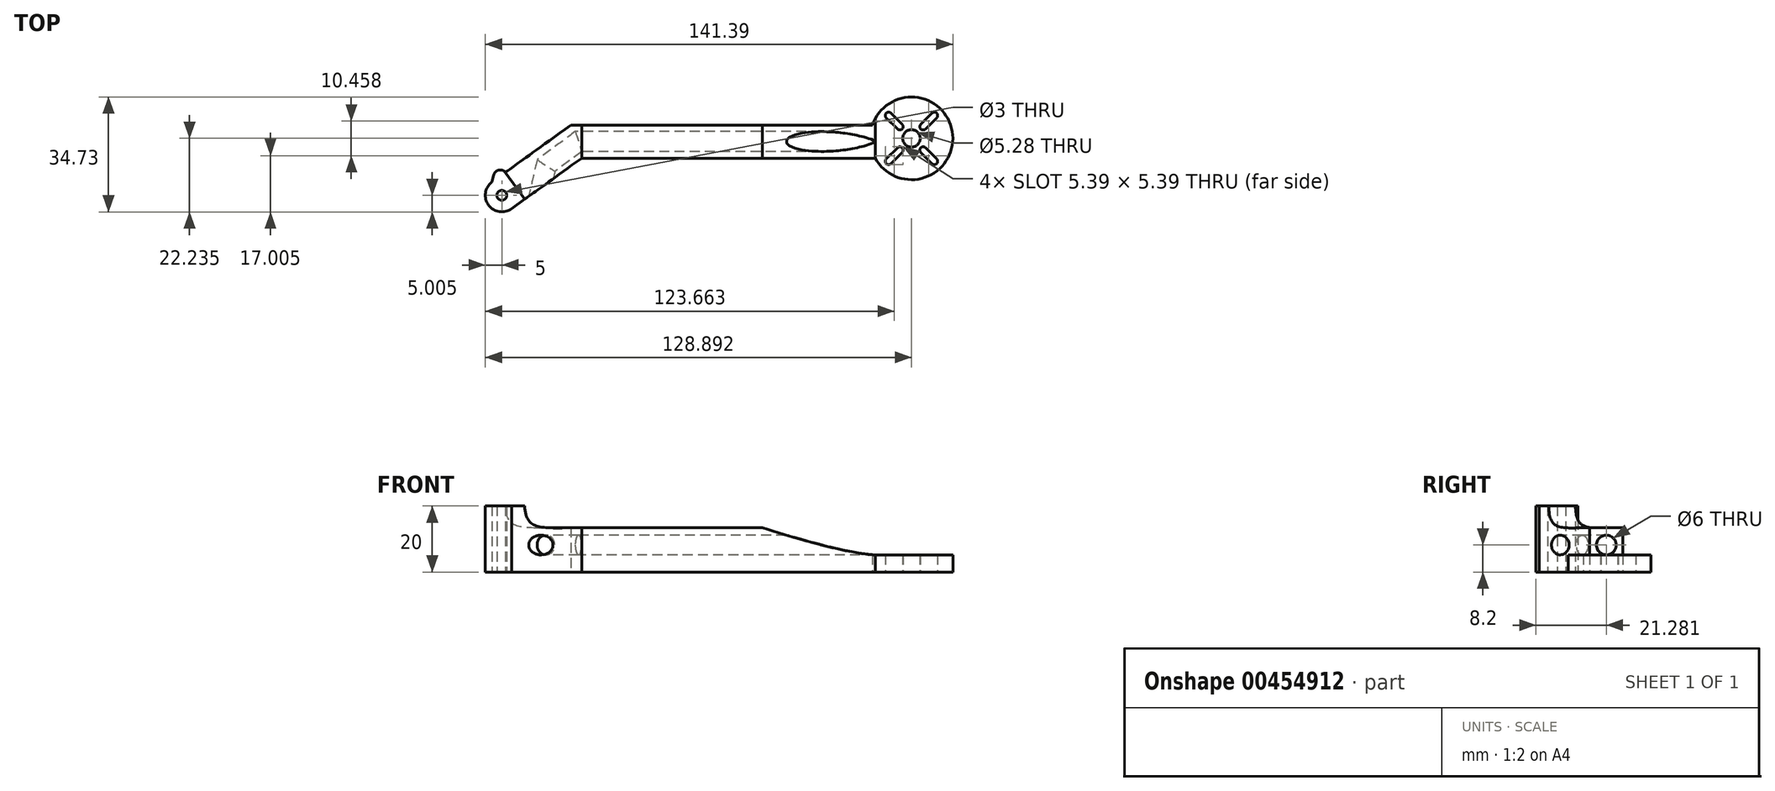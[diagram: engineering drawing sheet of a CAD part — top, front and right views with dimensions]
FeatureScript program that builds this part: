
annotation { "Feature Type Name" : "Feature", "Feature Type Description" : "" }
export const myFeature = defineFeature(function(context is Context, id is Id, definition is map)
    precondition{}
    {
        {
            var Q0;
            Q0=qCreatedBy(makeId("Top.planeOp"),FACE);
            var sketch = newSketch(context, id + "F0", { "sketchPlane" : qUnion([Q0])});
            skLineSegment(sketch, "E0", {"start": v(-161.05, 41.93) * mm, "end": v(-137.16, 59.15) * mm, "construction": true});
            skLineSegment(sketch, "E1", {"start": v(-137.16, 59.15) * mm, "end": v(-37.16, 59.15) * mm, "construction": true});
            skArc(sketch, "E2", {"start": v(-48.13, 53.17) * mm, "mid": v(-24.7, 60.23) * mm, "end": v(-49, 63.17) * mm});
            skLineSegment(sketch, "E3.0", {"start": v(-158.07, 37.9) * mm, "end": v(-136.9, 53.17) * mm});
            skLineSegment(sketch, "E4.0", {"start": v(-164.03, 45.94) * mm, "end": v(-140.14, 63.17) * mm});
            skArc(sketch, "E5", {"start": v(-164.03, 45.94) * mm, "mid": v(-165.07, 38.95) * mm, "end": v(-158.07, 37.9) * mm});
            skLineSegment(sketch, "E6", {"start": v(-140.14, 63.17) * mm, "end": v(-49, 63.17) * mm});
            skLineSegment(sketch, "E7", {"start": v(-136.9, 53.17) * mm, "end": v(-48.13, 53.17) * mm});
            skCircle(sketch, "E8", {"center": v(-37.16, 59.15) * mm, "radius": 2.64 * mm});
            skArc(sketch, "E9.0.startCap", {"start": v(-44.79, 65.37) * mm, "mid": v(-44.79, 66.78) * mm, "end": v(-43.37, 66.78) * mm});
            skArc(sketch, "E9.0.endCap", {"start": v(-39.99, 63.4) * mm, "mid": v(-39.99, 61.98) * mm, "end": v(-41.4, 61.98) * mm});
            skLineSegment(sketch, "E9.0.left", {"start": v(-43.37, 66.78) * mm, "end": v(-39.99, 63.4) * mm});
            skLineSegment(sketch, "E9.0.right", {"start": v(-44.79, 65.37) * mm, "end": v(-41.4, 61.98) * mm});
            skLineSegment(sketch, "E10", {"start": v(-37.16, 59.15) * mm, "end": v(-37.16, 66.76) * mm, "construction": true});
            skArc(sketch, "E11.MirrorCS", {"start": v(-29.53, 65.37) * mm, "mid": v(-29.53, 66.78) * mm, "end": v(-30.94, 66.78) * mm});
            skArc(sketch, "E12.MirrorCS", {"start": v(-34.33, 63.4) * mm, "mid": v(-34.33, 61.98) * mm, "end": v(-32.92, 61.98) * mm});
            skLineSegment(sketch, "E13.MirrorCS", {"start": v(-29.53, 65.37) * mm, "end": v(-32.92, 61.98) * mm});
            skLineSegment(sketch, "E14.MirrorCS", {"start": v(-30.94, 66.78) * mm, "end": v(-34.33, 63.4) * mm});
            skLineSegment(sketch, "E15.MirrorCS", {"start": v(-30.94, 51.52) * mm, "end": v(-34.33, 54.91) * mm});
            skArc(sketch, "E16.MirrorCS", {"start": v(-29.53, 52.94) * mm, "mid": v(-29.53, 51.52) * mm, "end": v(-30.94, 51.52) * mm});
            skLineSegment(sketch, "E17.MirrorCS", {"start": v(-29.53, 52.94) * mm, "end": v(-32.92, 56.33) * mm});
            skArc(sketch, "E18.MirrorCS", {"start": v(-34.33, 54.91) * mm, "mid": v(-34.33, 56.33) * mm, "end": v(-32.92, 56.33) * mm});
            skLineSegment(sketch, "E19.MirrorCS", {"start": v(-44.79, 52.94) * mm, "end": v(-41.4, 56.33) * mm});
            skLineSegment(sketch, "E20.MirrorCS", {"start": v(-43.37, 51.52) * mm, "end": v(-39.99, 54.91) * mm});
            skArc(sketch, "E21.MirrorCS", {"start": v(-39.99, 54.91) * mm, "mid": v(-39.99, 56.33) * mm, "end": v(-41.4, 56.33) * mm});
            skArc(sketch, "E22.MirrorCS", {"start": v(-44.79, 52.94) * mm, "mid": v(-44.79, 51.52) * mm, "end": v(-43.37, 51.52) * mm});
            skCircle(sketch, "E23", {"center": v(-161.05, 41.93) * mm, "radius": 1.5 * mm});
            skLineSegment(sketch, "E24", {"start": v(-37.16, 59.15) * mm, "end": v(-44.76, 66.76) * mm, "construction": true});
            skSolve(sketch);
        }
        {
            var Q0;
            Q0 = qSketchRegion(id + "F0", true);
            extrude(context, id + "F1", {"entities" : qUnion([Q0]), "depth" : 20 * mm});
        }
        {
            var Q0;
            Q0=makeQuery(id+"F1.opExtrude","SWEPT_FACE",FACE,{"disambiguationData":[OSD([sQuery(id+"F0.wireOp",EDGE,"E7")])]});
            var sketch = newSketch(context, id + "F2", { "sketchPlane" : qUnion([Q0])});
            skFitSpline(sketch, "E25", {"points": [v(-48.13, 5.2) * mm, v(-101.02, 20) * mm], "startDerivative": vector(-37.65, 1.6) * mm, "endDerivative": vector(-23.18, 9.57) * mm});
            skLineSegment(sketch, "E26", {"start": v(-48.13, 5.2) * mm, "end": v(-22.68, 5.2) * mm});
            skLineSegment(sketch, "E27", {"start": v(-22.68, 5.2) * mm, "end": v(-24.44, 23.02) * mm});
            skLineSegment(sketch, "E28", {"start": v(-24.44, 23.02) * mm, "end": v(-102.95, 23.97) * mm});
            skLineSegment(sketch, "E29", {"start": v(-102.95, 23.97) * mm, "end": v(-109.86, 20) * mm});
            skLineSegment(sketch, "E30", {"start": v(-82.25, 13.43) * mm, "end": v(-136.9, 13.43) * mm});
            skLineSegment(sketch, "E31", {"start": v(-136.9, 13.43) * mm, "end": v(-136.9, 24.34) * mm});
            skLineSegment(sketch, "E32", {"start": v(-136.9, 24.34) * mm, "end": v(-109.86, 20) * mm});
            skSolve(sketch);
        }
        {
            var Q0;
            Q0 = qSketchRegion(id + "F2", true);
            extrude(context, id + "F3", {"entities" : qUnion([Q0]), "operationType" : NewBodyOperationType.REMOVE, "oppositeDirection" : true, "depth" : 25 * mm, "hasSecondDirection" : true, "secondDirectionOppositeDirection" : false, "secondDirectionDepth" : 25 * mm});
        }
        {
            var Q0;
            Q0=makeQuery(id+"F1.opExtrude","SWEPT_FACE",FACE,{"disambiguationData":[OSD([sQuery(id+"F0.wireOp",EDGE,"E4.0")])]});
            var sketch = newSketch(context, id + "F4", { "sketchPlane" : qUnion([Q0])});
            skPoint(sketch, "E33.0", {"position": v(74.1, 13.43) * mm});
            skLineSegment(sketch, "E34.0", {"start": v(106.17, 20) * mm, "end": v(76.72, 20) * mm, "construction": true});
            skFitSpline(sketch, "E35", {"points": [v(74.1, 13.43) * mm, v(101.18, 20) * mm], "startDerivative": vector(56.52, 1.22) * mm, "endDerivative": vector(1.22, 26.42) * mm});
            skLineSegment(sketch, "E36", {"start": v(74.1, 13.43) * mm, "end": v(73.63, 25.15) * mm});
            skLineSegment(sketch, "E37", {"start": v(73.63, 25.15) * mm, "end": v(97.88, 26.12) * mm});
            skLineSegment(sketch, "E38", {"start": v(97.88, 26.12) * mm, "end": v(101.18, 20) * mm});
            skSolve(sketch);
        }
        {
            var Q0;
            Q0 = qSketchRegion(id + "F4", true);
            extrude(context, id + "F5", {"entities" : qUnion([Q0]), "operationType" : NewBodyOperationType.REMOVE, "oppositeDirection" : true, "depth" : 25 * mm});
        }
        {
            var Q0;
            Q0=makeQuery(id+"F3.boolean.opBoolean","COPY",FACE,{"derivedFrom":makeQuery(id+"F3.opExtrude","SWEPT_FACE",FACE,{"disambiguationData":[OSD([sQuery(id+"F2.wireOp",EDGE,"E26")])]})});
            var sketch = newSketch(context, id + "F6", { "sketchPlane" : qUnion([Q0])});
            skLineSegment(sketch, "E39", {"start": v(-86.71, 58.17) * mm, "end": v(-61.2, 58.17) * mm});
            skLineSegment(sketch, "E40", {"start": v(-86.71, 58.17) * mm, "end": v(-137.85, 58.17) * mm});
            skLineSegment(sketch, "E41", {"start": v(-147.68, 50.92) * mm, "end": v(-156.98, 10.35) * mm});
            skLineSegment(sketch, "E42.trimOffspring", {"start": v(-147.68, 50.92) * mm, "end": v(-137.85, 58.17) * mm});
            skSolve(sketch);
        }
        {
            var Q0;
            Q0=makeQuery(id+"F3.boolean.opBoolean","COPY",EDGE,{"derivedFrom":makeQuery(id+"F3.opExtrude","SWEPT_EDGE",EDGE,{"disambiguationData":[OSD([sQuery(id+"F0.wireOp",EDGE,"E2"),sQuery(id+"F0.wireOp",EDGE,"E7"),sQuery(id+"F2.wireOp",EDGE,"E25"),sQuery(id+"F2.wireOp",EDGE,"E26")])]})});
            cPlane(context, id + "F7", {"entities" : qUnion([Q0]), "cplaneType" : CPlaneType.LINE_ANGLE, "offset" : 25 * mm, "angle" : 90 * degree, "width" : 150 * mm, "height" : 150 * mm});
        }
        {
            var Q0;
            Q0=qCreatedBy(id+"F7.planeOp",FACE);
            var sketch = newSketch(context, id + "F8", { "sketchPlane" : qUnion([Q0])});
            skLineSegment(sketch, "E43.0", {"start": v(65.14, 5.2) * mm, "end": v(53.17, 5.2) * mm, "construction": true});
            skCircle(sketch, "E44", {"center": v(58.2, 8.2) * mm, "radius": 3 * mm});
            skSolve(sketch);
        }
        {
            var Q0;
            Q0 = qSketchRegion(id + "F8", true);
            var Q1;
            Q1 = qConstructionFilter(qBodyType(qCreatedBy(id + "F6" ,EDGE), BodyType.WIRE), ConstructionObject.NO);
            sweep(context, id + "F9", {"operationType" : NewBodyOperationType.REMOVE, "profiles" : qUnion([Q0]), "path" : qUnion([Q1])});
        }
        {
            var Q0;
            Q0=makeQuery(id+"F1.opExtrude","CAP_FACE",FACE,{"disambiguationData":[OSD([sQuery(id+"F0.wireOp",EDGE,"E2"),sQuery(id+"F0.wireOp",EDGE,"E3.0"),sQuery(id+"F0.wireOp",EDGE,"E4.0"),sQuery(id+"F0.wireOp",EDGE,"E5"),sQuery(id+"F0.wireOp",EDGE,"E6"),sQuery(id+"F0.wireOp",EDGE,"E7"),sQuery(id+"F0.wireOp",EDGE,"E8"),sQuery(id+"F0.wireOp",EDGE,"E9.0.startCap"),sQuery(id+"F0.wireOp",EDGE,"E9.0.endCap"),sQuery(id+"F0.wireOp",EDGE,"E9.0.left"),sQuery(id+"F0.wireOp",EDGE,"E9.0.right"),sQuery(id+"F0.wireOp",EDGE,"E11.MirrorCS"),sQuery(id+"F0.wireOp",EDGE,"E12.MirrorCS"),sQuery(id+"F0.wireOp",EDGE,"E13.MirrorCS"),sQuery(id+"F0.wireOp",EDGE,"E14.MirrorCS"),sQuery(id+"F0.wireOp",EDGE,"E15.MirrorCS"),sQuery(id+"F0.wireOp",EDGE,"E16.MirrorCS"),sQuery(id+"F0.wireOp",EDGE,"E17.MirrorCS"),sQuery(id+"F0.wireOp",EDGE,"E18.MirrorCS"),sQuery(id+"F0.wireOp",EDGE,"E19.MirrorCS"),sQuery(id+"F0.wireOp",EDGE,"E20.MirrorCS"),sQuery(id+"F0.wireOp",EDGE,"E21.MirrorCS"),sQuery(id+"F0.wireOp",EDGE,"E22.MirrorCS"),sQuery(id+"F0.wireOp",EDGE,"E23")])],"isStart":true});
            var sketch = newSketch(context, id + "F10", { "sketchPlane" : qUnion([Q0])});
            skLineSegment(sketch, "E45", {"start": v(-164.03, -45.94) * mm, "end": v(-159.98, -48.86) * mm});
            skLineSegment(sketch, "E46", {"start": v(-159.98, -48.86) * mm, "end": v(-162.43, -52.25) * mm});
            skLineSegment(sketch, "E47", {"start": v(-162.43, -52.25) * mm, "end": v(-164.03, -45.94) * mm});
            skPoint(sketch, "E48.0", {"position": v(-159.98, -48.86) * mm});
            skSolve(sketch);
        }
        {
            var Q0;
            Q0=makeQuery(id+"F10.imprint","IMPRINT",FACE,{"disambiguationData":[TD([[makeQuery(id+"F10.imprint","IMPRINT",EDGE,{"derivedFrom":sQuery(id+"F10.wireOp",EDGE,"E45")}),-1.0]])]});
            extrude(context, id + "F11", {"entities" : qUnion([Q0]), "operationType" : NewBodyOperationType.ADD, "oppositeDirection" : true, "depth" : 20 * mm});
        }
        {
            var Q0;
            Q0=makeQuery(id+"F11.opExtrude","SWEPT_EDGE",EDGE,{"disambiguationData":[OSD([sQuery(id+"F10.wireOp",EDGE,"E46"),sQuery(id+"F10.wireOp",EDGE,"E47")])]});
            fillet(context, id + "F12", {"entities" : qUnion([Q0]), "radius" : 2 * mm, "tangentPropagation" : true, "allowEdgeOverflow" : false});
        }
    });
